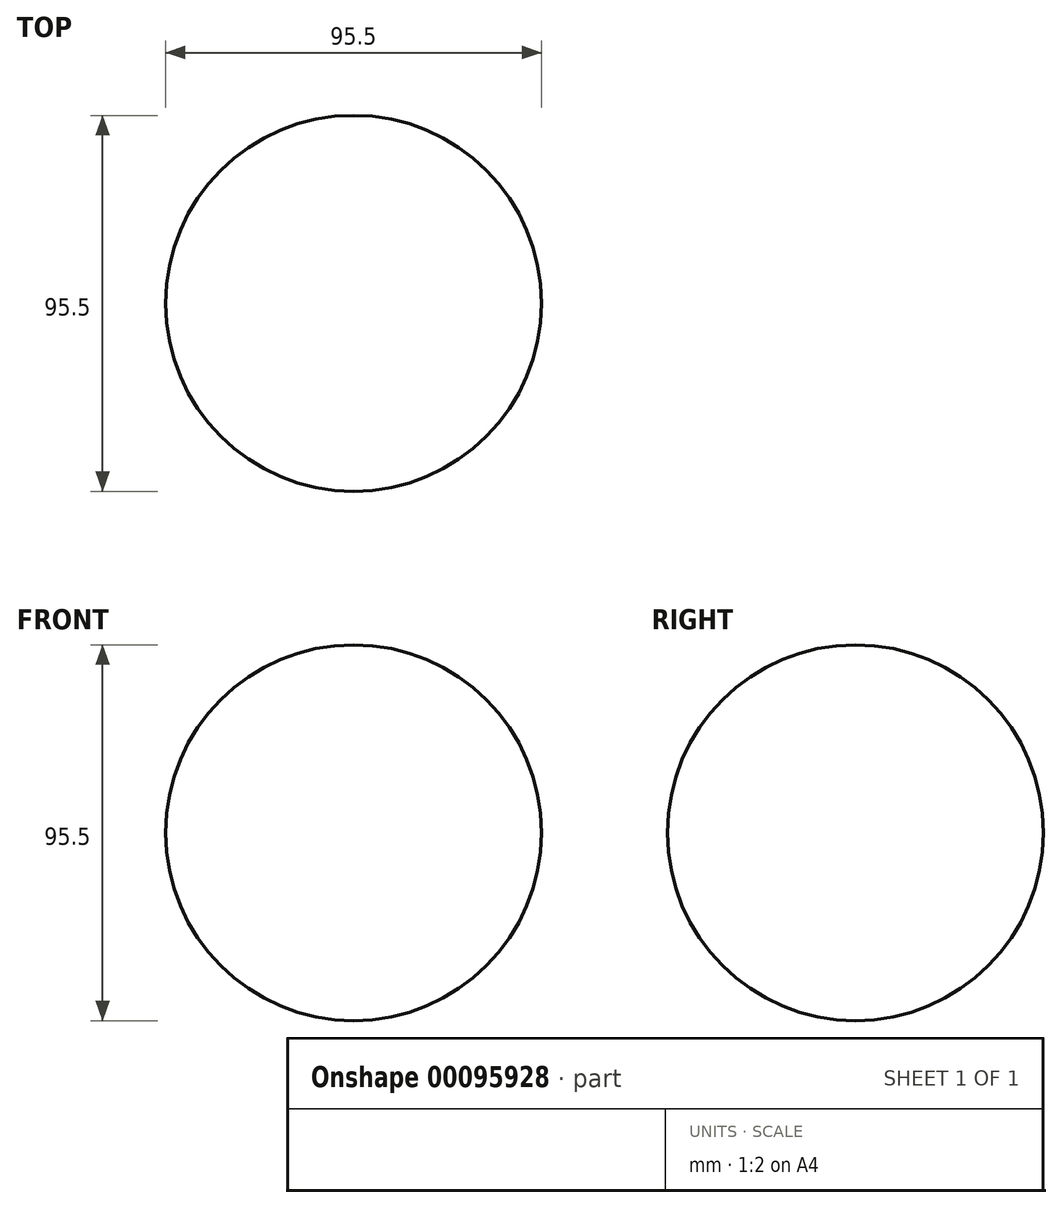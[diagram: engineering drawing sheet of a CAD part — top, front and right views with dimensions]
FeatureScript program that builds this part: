
annotation { "Feature Type Name" : "Feature", "Feature Type Description" : "" }
export const myFeature = defineFeature(function(context is Context, id is Id, definition is map)
    precondition{}
    {
        {
            var Q0;
            Q0=qCreatedBy(makeId("Front.planeOp"),FACE);
            var sketch = newSketch(context, id + "F0", { "sketchPlane" : qUnion([Q0])});
            skCircle(sketch, "E0", {"center": v(0, 0) * mm, "radius": 47.75 * mm});
            skLineSegment(sketch, "E1", {"start": v(0, -47.75) * mm, "end": v(0, 47.75) * mm});
            skSolve(sketch);
        }
        {
            var Q0;
            {var subQ0=sQuery(id+"F0.wireOp",EDGE,"E1");Q0=makeQuery(id+"F0.imprint","IMPRINT",FACE,{"disambiguationData":[TD([[makeQuery(id+"F0.imprint","IMPRINT",EDGE,{"derivedFrom":subQ0}),1.0]])]});}
            var Q1;
            Q1=sQuery(id+"F0.wireOp",EDGE,"E1");
            revolve(context, id + "F2", {"entities" : qUnion([Q0]), "axis" : qUnion([Q1]), "revolveType" : RevolveType.FULL});
        }
        {
            var Q0;
            Q0=qCreatedBy(makeId("Front.planeOp"),FACE);
            var sketch = newSketch(context, id + "F1", { "sketchPlane" : qUnion([Q0])});
            skLineSegment(sketch, "E2.bottom", {"start": v(20.95, -15.85) * mm, "end": v(-20.95, -15.85) * mm});
            skLineSegment(sketch, "E2.top", {"start": v(20.95, 15.85) * mm, "end": v(-20.95, 15.85) * mm});
            skLineSegment(sketch, "E2.left", {"start": v(20.95, -15.85) * mm, "end": v(20.95, 15.85) * mm});
            skLineSegment(sketch, "E2.right", {"start": v(-20.95, -15.85) * mm, "end": v(-20.95, 15.85) * mm});
            skPoint(sketch, "E2.middle", {"position": v(0, 0) * mm});
            skSolve(sketch);
        }
        {
            var Q0;
            Q0=sQuery(id+"F1.wireOp",EDGE,"E2.left");
            var Q1;
            Q1=sQuery(id+"F1.wireOp",EDGE,"E2.top");
            var Q2;
            Q2=sQuery(id+"F1.wireOp",EDGE,"E2.bottom");
            var Q3;
            Q3=sQuery(id+"F1.wireOp",EDGE,"E2.right");
            extrude(context, id + "F3", {"bodyType" : ToolBodyType.SURFACE, "surfaceEntities" : qUnion([Q0, Q1, Q2, Q3]), "depth" : 49.24 * mm});
        }
    });
